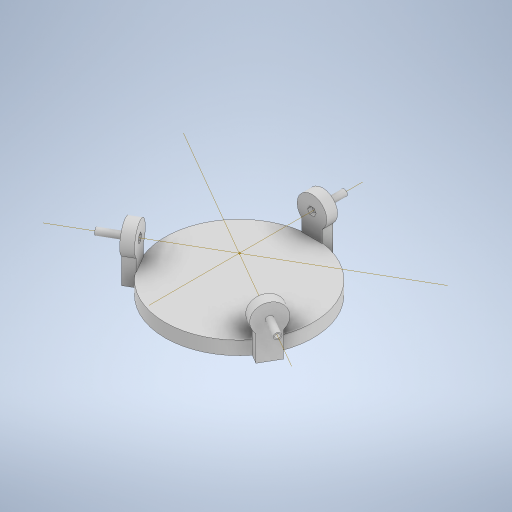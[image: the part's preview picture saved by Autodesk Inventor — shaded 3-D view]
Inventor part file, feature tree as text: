
AUTODESK INVENTOR PART (.ipt)
format: ipt  version: 2024 (Build 280153000, 153)  size: 347,136 bytes
history: native  units: mm
features: extrude x6, sketch x6, other x4, pattern_circular x3, projected_geometry x1
ambient origin geometry x8: Origin, YZ Plane, XZ Plane, XY Plane, X Axis, Y Axis, Z Axis, Center Point
bodies: Solid1 (feature_tree)
feature tree (20):
  extrude  "Extrusion1"  Depth=10.0mm TaperAngle=0.0deg
  extrude  "Extrusion2"  Depth=8.046738mm
  extrude  "Extrusion3"  Depth=5.0mm TaperAngle=0.0deg
  pattern_circular  "Circular Pattern1"  Count=3 Angle=360.0deg
  extrude  "Extrusion5"  Depth=10.0mm
  pattern_circular  "Circular Pattern3"  [2 undecoded]
  other  "Work Axis4"
  other  "Work Axis5"
  other  "Work Point2"
  extrude  "Extrusion6"  Depth=3.0mm TaperAngle=360.0deg
  extrude  "Extrusion7"  Depth=5.5mm
  pattern_circular  "Circular Pattern4"  [2 undecoded]
  sketch  "Sketch1"  dims[d0=110.0mm d1=10.0mm d2=0.0mm]
  sketch  "Sketch2"  dims[d3=15.0mm d4=8.046738mm]
  sketch  "Sketch3"  dims[d5=5.0mm d6=0.0mm d13=5.0mm d14=0.0mm d15=30.0mm d16=360.0deg]
  sketch  "Sketch5"  dims[d19=10.0mm d20=0.0mm d21=62.046738mm]
  other  "Work Axis6"
  sketch  "Sketch6"  dims[d27=22.0mm d28=12.0mm d29=15.0mm]
  sketch  "Sketch7"  dims[d30=4.8mm d31=24.0mm d32=0.0mm d33=30.0mm d34=360.0deg d36=5.5mm d37=3.0mm d38=0.0mm d39=3.2mm d40=0.0mm d41=0.0mm d42=30.0mm d43=360.0deg d22=0.0mm d23=0.0mm d24=0.0mm d25=0.872665mm]
  projected_geometry  "Projected Loop1"
note: 4 required parameter values undecoded (feature->parameter linkage not recoverable at this tier; creation-order binding heuristic only, values carry confidence <= 0.55)
